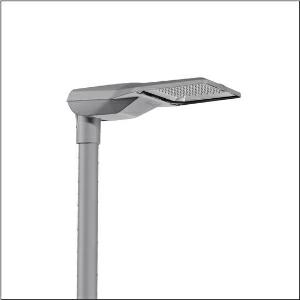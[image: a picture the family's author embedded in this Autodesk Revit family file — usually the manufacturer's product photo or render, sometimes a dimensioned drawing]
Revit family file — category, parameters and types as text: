
# Revit family: streetlight_sl_21_iq_midi___stw1_0a_5xe3e61g08nb_0b2e
name_source: partatom
category: Lighting Fixtures
units: mm (PartAtom-declared; Revit-internal decimal feet)

## family parameters
Cut with Voids When Loaded = No
Host = Face
Light Source = No
Part Type = Normal
Room Calculation Point = No
Round Connector Dimension = Use Diameter
Shared = No

## types (1)
- --- (1 x LED, 20820 lm, 155.5 W, 2700K)
    Apparent Load = 155 VA
    CIE Flux Codes = 39 75 98 100 100
    Color Rendering = 70
    Color Temperature = 2700K
    Default Elevation = 1800 mm
    Description = Streetlight SL 21 iQ midi, mast luminaire, primary light control with lens, of PMMA, primary optical cover: cover, of toughened safety glass, transparent, light distribution: STW1.0a, light emission: direct distribution, primary light characteristic: asymmetric, installation type: post-top, side-entry, LED, High Power LED, rated luminous flux: 20.820lm, luminous efficacy: 134lm/W, light colour: 727, colour temperature: 2700K, control: Street-Remote, Auto-Match, Temp-Guard, Lumen-Switch, Night-Set, Smart-Wire, Light-Fading, Desk-Remote (wireless, voltage-free reading and setting of iQ features in the workshop via application-optimized NFC function/RFID function), optimised constant luminous flux control (CLO 2.0), presetting dimming linear, mains connection: 230..240V, AC, 50/60Hz, start of lifetime: 156W, end of service life: 162W, reduction: 69W, luminaire housing, of diecast aluminium, powder-coated, Siteco® metallic grey (DB 702S), corrosivity category C5 mid according to DIN EN ISO 12944, please order mast flange separately, inclination adjustable: 0°, 5°, 10°, 15°, sealing non-destructively replaceable, multi-level sealing system, length: 644mm, width: 335mm, height: 110mm, mast flange for spigot size: 42mm (side-entry): 5XC10008XM4, 60/48mm (side-entry/post-top): 5XC10108XM2, 76/60mm (side-entry/post-top): 5XC10108XM1, protection rating (complete): IP66, insulation class (complete): insulation class II (safety insulation), certification: CE, ENEC, ENEC+, VDE, impact resistance: IK09, permissible operating ambient temperature for outdoor applications: -40..+50°C, standard-compliant lighting for roads and squares, packaging unit: 1 piece

Light Distribution: STW1.0a
    Height = 111 mm
    Lamp = 1 x LED
    Lamp Light Flux = 20820 lm
    Lamp Power = 155.5 W
    Lamp count = 1
    Length = 644 mm
    Luminous efficacy = 134 lm/W
    Manufacturer = Siteco
    ModVariant = No
    Model = 5XE3E61G08NB
    Number of Poles = 1
    OnlyDefault = Yes
    Power Factor = 1
    Product Name = Streetlight SL 21 iQ midi | STW1.0a
    Product group = mast luminaire | pylon top
    ProductGroupID = 6100
    Protection Class = Protection class II
    Protection Degree = IP 66
    RLX_Detail_Level = 1
    RLX_Emergency_Light_Flux = 0 lm
    RLX_Emergency_Type = 0
    RLX_Emergency_Type_DB = No
    RlxData = <blob elided: 90857 chars, md5=bd85c785>
    Socket = socket
    Standby Power = 0 W
    System Light Flux = 20820 lm
    System Power = 155 W
    Type Comments = factory setting: luminous flux: 100 % | dim-lin: 254 | 823 mA
    Type Image = l_1004298.jpg
    URL = http://relux.com
    VarID = @adj_102305
    Voltage = 0 V
    Weight = 0.00 kg
    Width = 336 mm

## geometry (parser evidence)
native form markers: Blend x4, Sweep x10
no freeform markers — native parametric forms only
